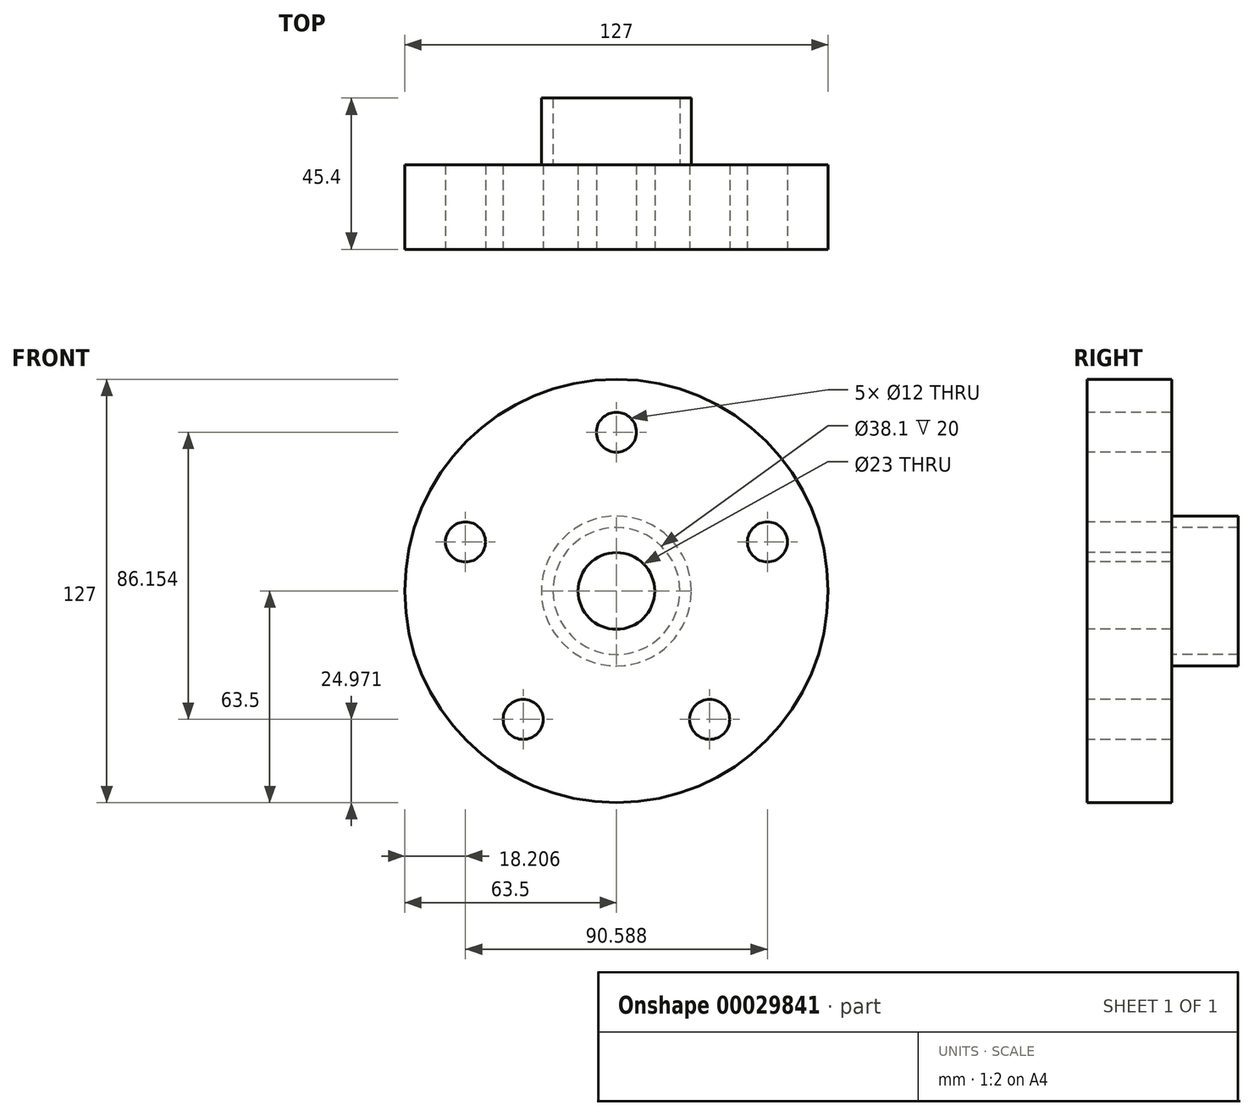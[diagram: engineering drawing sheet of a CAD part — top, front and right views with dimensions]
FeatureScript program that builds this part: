
annotation { "Feature Type Name" : "Feature", "Feature Type Description" : "" }
export const myFeature = defineFeature(function(context is Context, id is Id, definition is map)
    precondition{}
    {
        {
            var Q0;
            Q0=qCreatedBy(makeId("Front.planeOp"),FACE);
            var sketch = newSketch(context, id + "F0", { "sketchPlane" : qUnion([Q0])});
            skCircle(sketch, "E0", {"center": v(0, 0) * mm, "radius": 63.5 * mm});
            skSolve(sketch);
        }
        {
            var Q0;
            Q0 = qSketchRegion(id + "F0", true);
            extrude(context, id + "F1", {"entities" : qUnion([Q0]), "depth" : 25.4 * mm});
        }
        {
            var Q0;
            Q0=makeQuery(id+"F1.opExtrude","CAP_FACE",FACE,{"disambiguationData":[OSD([sQuery(id+"F0.wireOp",EDGE,"E0")])],"isStart":true});
            var sketch = newSketch(context, id + "F2", { "sketchPlane" : qUnion([Q0])});
            skCircle(sketch, "E1", {"center": v(0, 0) * mm, "radius": 22.5 * mm});
            skCircle(sketch, "E2", {"center": v(0, 0) * mm, "radius": 19.05 * mm});
            skSolve(sketch);
        }
        {
            var Q0;
            Q0 = qSketchRegion(id + "F2", true);
            extrude(context, id + "F3", {"entities" : qUnion([Q0]), "operationType" : NewBodyOperationType.ADD, "depth" : 20 * mm});
        }
        {
            var Q0;
            Q0=makeQuery(id+"F1.opExtrude","CAP_FACE",FACE,{"disambiguationData":[OSD([sQuery(id+"F0.wireOp",EDGE,"E0")])],"isStart":false});
            var sketch = newSketch(context, id + "F4", { "sketchPlane" : qUnion([Q0])});
            skCircle(sketch, "E3", {"center": v(0, 0) * mm, "radius": 11.5 * mm});
            skSolve(sketch);
        }
        {
            var Q0;
            Q0 = qSketchRegion(id + "F4", true);
            extrude(context, id + "F5", {"entities" : qUnion([Q0]), "operationType" : NewBodyOperationType.REMOVE, "endBound" : BoundingType.UP_TO_NEXT, "oppositeDirection" : true, "depth" : 25.4 * mm});
        }
        {
            var Q0;
            Q0=makeQuery(id+"F1.opExtrude","CAP_FACE",FACE,{"disambiguationData":[OSD([sQuery(id+"F0.wireOp",EDGE,"E0")])],"isStart":false});
            var sketch = newSketch(context, id + "F6", { "sketchPlane" : qUnion([Q0])});
            skCircle(sketch, "E4", {"center": v(0, 0) * mm, "radius": 47.63 * mm, "construction": true});
            skCircle(sketch, "E5", {"center": v(0, 47.63) * mm, "radius": 6 * mm});
            skCircle(sketch, "E6.1.0", {"center": v(-45.3, 14.72) * mm, "radius": 6 * mm});
            skCircle(sketch, "E6.2.0", {"center": v(-28, -38.53) * mm, "radius": 6 * mm});
            skCircle(sketch, "E6.3.0", {"center": v(28, -38.53) * mm, "radius": 6 * mm});
            skCircle(sketch, "E6.4.0", {"center": v(45.3, 14.72) * mm, "radius": 6 * mm});
            skSolve(sketch);
        }
        {
            var Q0;
            Q0 = qSketchRegion(id + "F6", true);
            extrude(context, id + "F7", {"entities" : qUnion([Q0]), "operationType" : NewBodyOperationType.REMOVE, "endBound" : BoundingType.UP_TO_NEXT, "oppositeDirection" : true, "depth" : 25 * mm});
        }
    });
